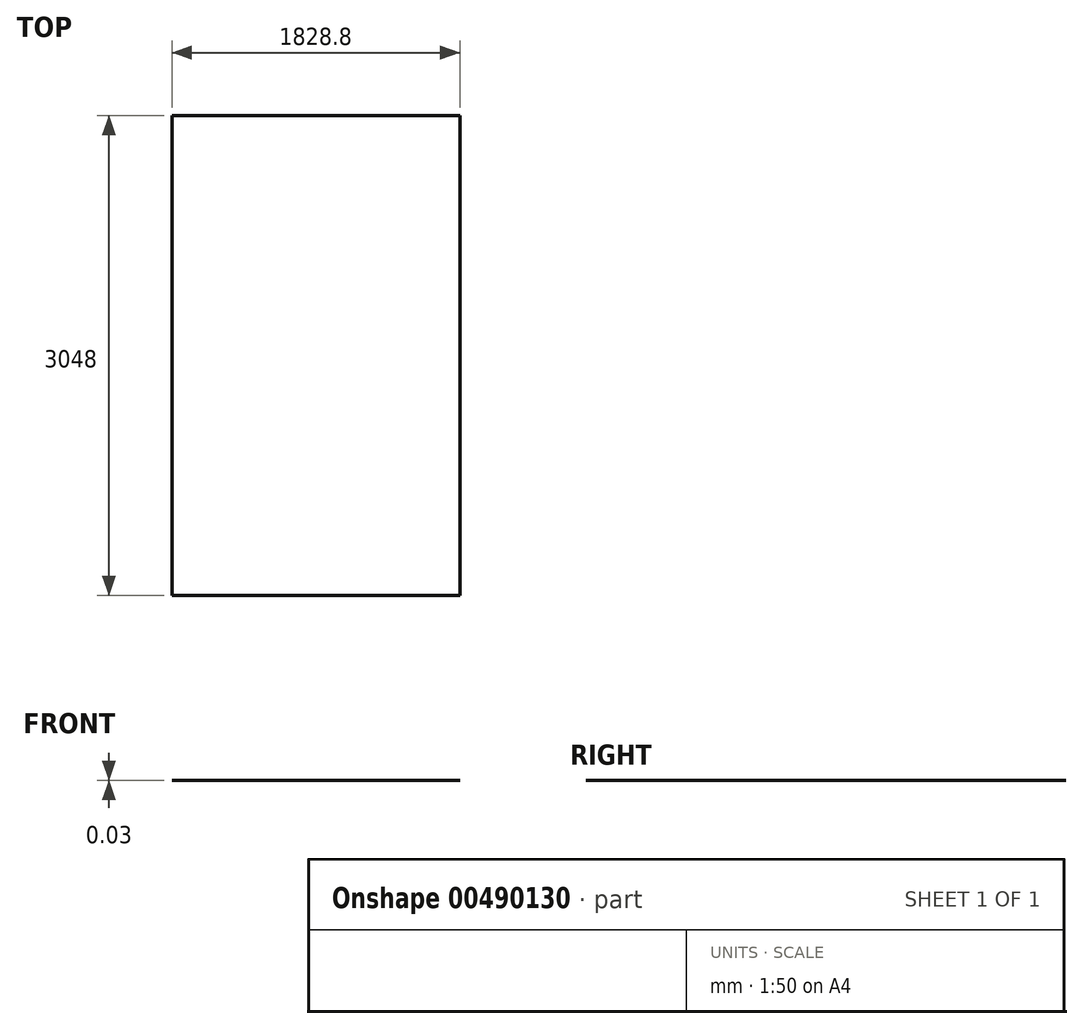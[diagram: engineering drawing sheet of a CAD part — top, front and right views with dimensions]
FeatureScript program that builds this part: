
annotation { "Feature Type Name" : "Feature", "Feature Type Description" : "" }
export const myFeature = defineFeature(function(context is Context, id is Id, definition is map)
    precondition{}
    {
        {
            var Q0;
            Q0=qCreatedBy(makeId("Top.planeOp"),FACE);
            var sketch = newSketch(context, id + "F0", { "sketchPlane" : qUnion([Q0])});
            skLineSegment(sketch, "E0.bottom", {"start": v(914.4, -1524) * mm, "end": v(-914.4, -1524) * mm});
            skLineSegment(sketch, "E0.top", {"start": v(914.4, 1524) * mm, "end": v(-914.4, 1524) * mm});
            skLineSegment(sketch, "E0.left", {"start": v(914.4, -1524) * mm, "end": v(914.4, 1524) * mm});
            skLineSegment(sketch, "E0.right", {"start": v(-914.4, -1524) * mm, "end": v(-914.4, 1524) * mm});
            skPoint(sketch, "E0.middle", {"position": v(0, 0) * mm});
            skSolve(sketch);
        }
        {
            var Q0;
            Q0 = qSketchRegion(id + "F0", true);
            extrude(context, id + "F1", {"entities" : qUnion([Q0]), "depth" : 0.03 * mm, "offsetDistance" : 25.4 * mm});
        }
    });
